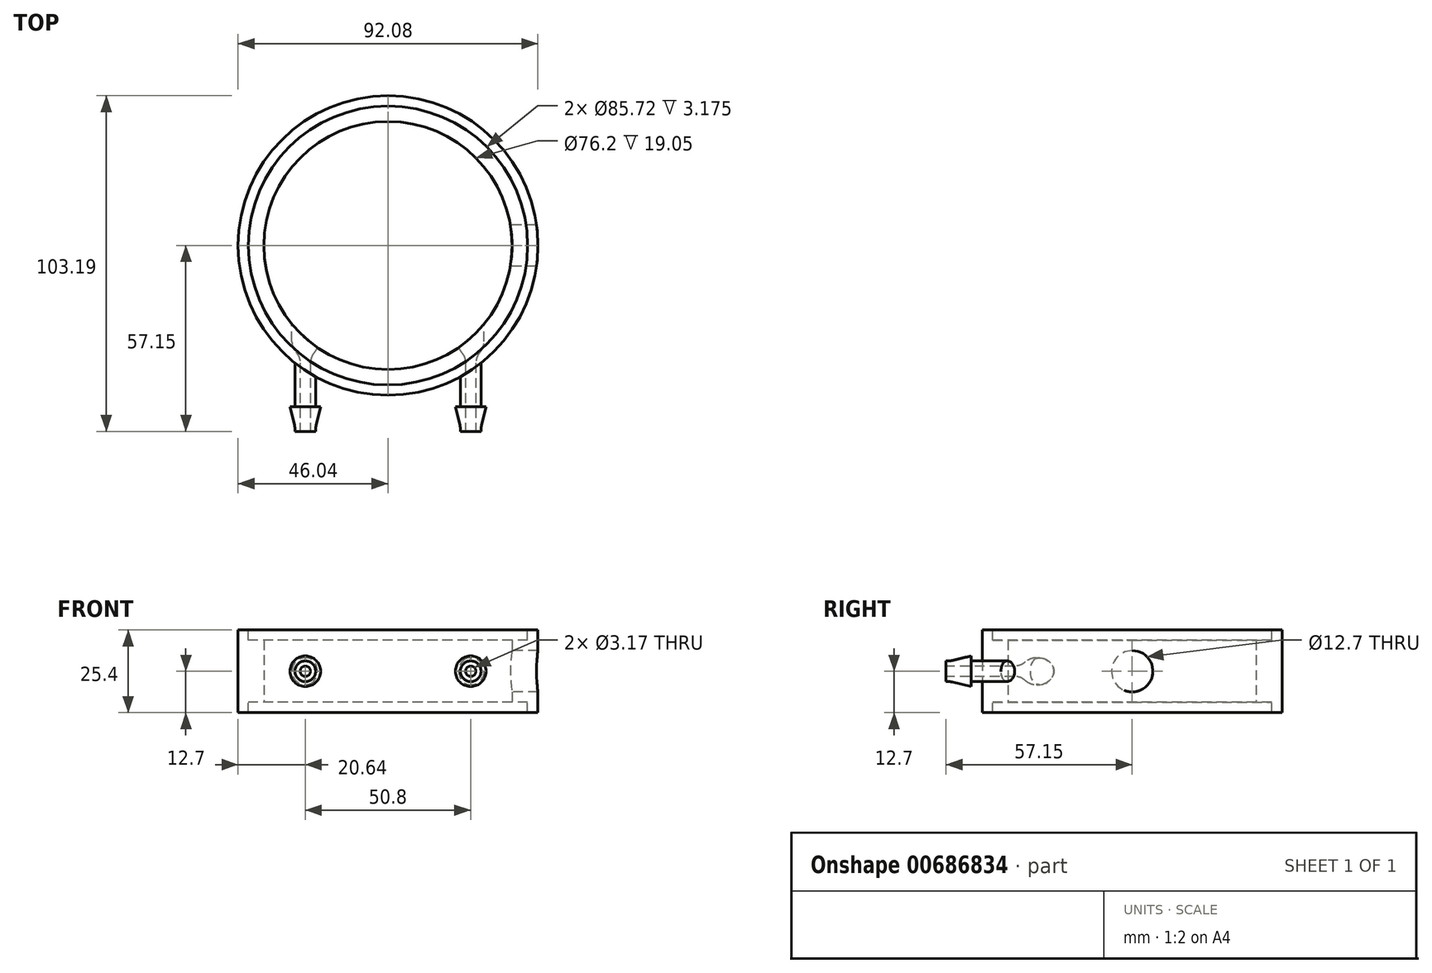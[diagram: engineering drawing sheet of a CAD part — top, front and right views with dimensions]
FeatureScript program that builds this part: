
annotation { "Feature Type Name" : "Feature", "Feature Type Description" : "" }
export const myFeature = defineFeature(function(context is Context, id is Id, definition is map)
    precondition{}
    {
        {
            var Q0;
            Q0=qCreatedBy(makeId("Top.planeOp"),FACE);
            var sketch = newSketch(context, id + "F0", { "sketchPlane" : qUnion([Q0])});
            skCircle(sketch, "E0", {"center": v(0, 0) * mm, "radius": 46.04 * mm});
            skSolve(sketch);
        }
        {
            var Q0;
            Q0 = qSketchRegion(id + "F0", true);
            extrude(context, id + "F1", {"entities" : qUnion([Q0]), "endBound" : BoundingType.SYMMETRIC, "depth" : 25.4 * mm, "offsetDistance" : 25.4 * mm});
        }
        {
            var Q0;
            Q0=qCreatedBy(makeId("Top.planeOp"),FACE);
            var sketch = newSketch(context, id + "F2", { "sketchPlane" : qUnion([Q0])});
            skCircle(sketch, "E1", {"center": v(0, 0) * mm, "radius": 42.86 * mm});
            skSolve(sketch);
        }
        {
            var Q0;
            Q0 = qSketchRegion(id + "F2", true);
            extrude(context, id + "F3", {"entities" : qUnion([Q0]), "operationType" : NewBodyOperationType.REMOVE, "endBound" : BoundingType.SYMMETRIC, "oppositeDirection" : true, "depth" : 25.4 * mm, "offsetDistance" : 25.4 * mm});
        }
        {
            var Q0;
            Q0=qCreatedBy(makeId("Top.planeOp"),FACE);
            var sketch = newSketch(context, id + "F4", { "sketchPlane" : qUnion([Q0])});
            skCircle(sketch, "E2", {"center": v(0, 0) * mm, "radius": 42.86 * mm});
            skSolve(sketch);
        }
        {
            var Q0;
            Q0 = qSketchRegion(id + "F4", true);
            extrude(context, id + "F5", {"entities" : qUnion([Q0]), "operationType" : NewBodyOperationType.ADD, "endBound" : BoundingType.SYMMETRIC, "depth" : 19.05 * mm, "offsetDistance" : 25.4 * mm});
        }
        {
            var Q0;
            Q0=qCreatedBy(makeId("Top.planeOp"),FACE);
            var sketch = newSketch(context, id + "F6", { "sketchPlane" : qUnion([Q0])});
            skCircle(sketch, "E3", {"center": v(0, 0) * mm, "radius": 38.1 * mm});
            skSolve(sketch);
        }
        {
            var Q0;
            Q0=qCreatedBy(makeId("Front.planeOp"),FACE);
            var sketch = newSketch(context, id + "F7", { "sketchPlane" : qUnion([Q0])});
            skCircle(sketch, "E4", {"center": v(-25.4, 0) * mm, "radius": 3.18 * mm});
            skSolve(sketch);
        }
        {
            var Q0;
            Q0=qCreatedBy(makeId("Front.planeOp"),FACE);
            var sketch = newSketch(context, id + "F8", { "sketchPlane" : qUnion([Q0])});
            skCircle(sketch, "E5", {"center": v(25.4, 0) * mm, "radius": 3.18 * mm});
            skSolve(sketch);
        }
        {
            var Q0;
            Q0 = qSketchRegion(id + "F7", true);
            extrude(context, id + "F9", {"entities" : qUnion([Q0]), "operationType" : NewBodyOperationType.ADD, "depth" : 57.15 * mm, "offsetDistance" : 25.4 * mm});
        }
        {
            var Q0;
            Q0 = qSketchRegion(id + "F8", true);
            extrude(context, id + "F10", {"entities" : qUnion([Q0]), "operationType" : NewBodyOperationType.ADD, "depth" : 57.15 * mm, "offsetDistance" : 25.4 * mm});
        }
        {
            var Q0;
            Q0=makeQuery(id+"F9.opExtrude","CAP_FACE",FACE,{"disambiguationData":[OSD([sQuery(id+"F7.wireOp",EDGE,"E4")])],"isStart":false});
            var sketch = newSketch(context, id + "F11", { "sketchPlane" : qUnion([Q0])});
            skCircle(sketch, "E6", {"center": v(-25.4, 0) * mm, "radius": 1.59 * mm});
            skSolve(sketch);
        }
        {
            var Q0;
            Q0=makeQuery(id+"F11.imprint","IMPRINT",FACE,{"disambiguationData":[TD([[makeQuery(id+"F11.imprint","IMPRINT",EDGE,{"derivedFrom":sQuery(id+"F11.wireOp",EDGE,"E6")}),1.0]])]});
            extrude(context, id + "F12", {"entities" : qUnion([Q0]), "operationType" : NewBodyOperationType.REMOVE, "oppositeDirection" : true, "depth" : 57.15 * mm, "offsetDistance" : 25.4 * mm});
        }
        {
            var Q0;
            Q0=makeQuery(id+"F10.opExtrude","CAP_FACE",FACE,{"disambiguationData":[OSD([sQuery(id+"F8.wireOp",EDGE,"E5")])],"isStart":false});
            var sketch = newSketch(context, id + "F13", { "sketchPlane" : qUnion([Q0])});
            skCircle(sketch, "E7", {"center": v(25.4, 0) * mm, "radius": 1.59 * mm});
            skSolve(sketch);
        }
        {
            var Q0;
            Q0=makeQuery(id+"F13.imprint","IMPRINT",FACE,{"disambiguationData":[TD([[makeQuery(id+"F13.imprint","IMPRINT",EDGE,{"derivedFrom":sQuery(id+"F13.wireOp",EDGE,"E7")}),1.0]])]});
            extrude(context, id + "F14", {"entities" : qUnion([Q0]), "operationType" : NewBodyOperationType.REMOVE, "oppositeDirection" : true, "depth" : 57.15 * mm, "offsetDistance" : 25.4 * mm});
        }
        {
            var Q0;
            Q0 = qSketchRegion(id + "F6", true);
            extrude(context, id + "F15", {"entities" : qUnion([Q0]), "operationType" : NewBodyOperationType.REMOVE, "endBound" : BoundingType.SYMMETRIC, "depth" : 25.4 * mm, "offsetDistance" : 25.4 * mm});
        }
        {
            var Q0;
            Q0=qCreatedBy(makeId("Top.planeOp"),FACE);
            var sketch = newSketch(context, id + "F16", { "sketchPlane" : qUnion([Q0])});
            skLineSegment(sketch, "E8", {"start": v(22.23, -49.53) * mm, "end": v(22.23, -55.88) * mm});
            skLineSegment(sketch, "E9", {"start": v(22.23, -49.53) * mm, "end": v(20.7, -49.53) * mm});
            skLineSegment(sketch, "E10", {"start": v(20.7, -49.53) * mm, "end": v(22.23, -55.88) * mm});
            skSolve(sketch);
        }
        {
            var Q0;
            Q0=makeQuery(id+"F16.imprint","IMPRINT",FACE,{"disambiguationData":[TD([[makeQuery(id+"F16.imprint","IMPRINT",EDGE,{"derivedFrom":sQuery(id+"F16.wireOp",EDGE,"E8")}),-1.0]])]});
            var Q1;
            Q1=makeQuery(id+"F10.opExtrude","CAP_EDGE",EDGE,{"disambiguationData":[OSD([sQuery(id+"F8.wireOp",EDGE,"E5")])],"isStart":false});
            revolve(context, id + "F17", {"operationType" : NewBodyOperationType.ADD, "entities" : qUnion([Q0]), "axis" : qUnion([Q1]), "revolveType" : RevolveType.FULL});
        }
        {
            var Q0;
            Q0=qCreatedBy(makeId("Top.planeOp"),FACE);
            var sketch = newSketch(context, id + "F18", { "sketchPlane" : qUnion([Q0])});
            skLineSegment(sketch, "E11", {"start": v(-22.23, -49.53) * mm, "end": v(-22.23, -55.88) * mm});
            skLineSegment(sketch, "E12", {"start": v(-22.23, -49.53) * mm, "end": v(-20.7, -49.53) * mm});
            skLineSegment(sketch, "E13", {"start": v(-20.7, -49.53) * mm, "end": v(-22.23, -55.88) * mm});
            skSolve(sketch);
        }
        {
            var Q0;
            Q0=makeQuery(id+"F18.imprint","IMPRINT",FACE,{"disambiguationData":[TD([[makeQuery(id+"F18.imprint","IMPRINT",EDGE,{"derivedFrom":sQuery(id+"F18.wireOp",EDGE,"E11")}),1.0]])]});
            var Q1;
            Q1=makeQuery(id+"F9.opExtrude","CAP_EDGE",EDGE,{"disambiguationData":[OSD([sQuery(id+"F7.wireOp",EDGE,"E4")])],"isStart":false});
            revolve(context, id + "F19", {"operationType" : NewBodyOperationType.ADD, "entities" : qUnion([Q0]), "axis" : qUnion([Q1]), "revolveType" : RevolveType.FULL});
        }
        {
            var Q0;
            Q0=makeQuery(id+"F19.opRevolve","SWEPT_EDGE",EDGE,{"disambiguationData":[OSD([sQuery(id+"F18.wireOp",EDGE,"E11"),sQuery(id+"F18.wireOp",EDGE,"E13")])]});
            fillet(context, id + "F20", {"entities" : qUnion([Q0]), "radius" : 5.08 * mm, "tangentPropagation" : true, "allowEdgeOverflow" : false});
        }
        {
            var Q0;
            Q0=makeQuery(id+"F17.opRevolve","SWEPT_EDGE",EDGE,{"disambiguationData":[OSD([sQuery(id+"F16.wireOp",EDGE,"E8"),sQuery(id+"F16.wireOp",EDGE,"E10")])]});
            fillet(context, id + "F21", {"entities" : qUnion([Q0]), "radius" : 5.08 * mm, "tangentPropagation" : true, "allowEdgeOverflow" : false});
        }
        {
            var Q0;
            Q0=qCreatedBy(makeId("Front.planeOp"),FACE);
            var sketch = newSketch(context, id + "F22", { "sketchPlane" : qUnion([Q0])});
            skCircle(sketch, "E14", {"center": v(-25.4, 0) * mm, "radius": 4.13 * mm});
            skSolve(sketch);
        }
        {
            var Q0;
            Q0=makeQuery(id+"F22.imprint","IMPRINT",FACE,{"disambiguationData":[TD([[makeQuery(id+"F22.imprint","IMPRINT",EDGE,{"derivedFrom":sQuery(id+"F22.wireOp",EDGE,"E14")}),1.0]])]});
            extrude(context, id + "F23", {"entities" : qUnion([Q0]), "operationType" : NewBodyOperationType.REMOVE, "depth" : 31.75 * mm, "offsetDistance" : 25.4 * mm});
        }
        {
            var Q0;
            Q0=makeQuery(id+"F23.boolean.opBoolean","INTERSECT",EDGE,{"derivedFrom":[makeQuery(id+"F12.boolean.opBoolean","COPY",FACE,{"derivedFrom":makeQuery(id+"F12.opExtrude","SWEPT_FACE",FACE,{"disambiguationData":[OSD([sQuery(id+"F11.wireOp",EDGE,"E6")])]})}),makeQuery(id+"F23.opExtrude","CAP_FACE",FACE,{"disambiguationData":[OSD([sQuery(id+"F22.wireOp",EDGE,"E14")])],"isStart":false})]});
            fillet(context, id + "F24", {"entities" : qUnion([Q0]), "radius" : 5.08 * mm, "tangentPropagation" : true, "allowEdgeOverflow" : false});
        }
        {
            var Q0;
            {var subQ0=sQuery(id+"F22.wireOp",EDGE,"E14");Q0=makeQuery(id+"F24.opFillet","BLEND_EDGE",EDGE,{"blendedFrom":[makeQuery(id+"F23.boolean.opBoolean","INTERSECT",EDGE,{"derivedFrom":[makeQuery(id+"F12.boolean.opBoolean","COPY",FACE,{"derivedFrom":makeQuery(id+"F12.opExtrude","SWEPT_FACE",FACE,{"disambiguationData":[OSD([sQuery(id+"F11.wireOp",EDGE,"E6")])]})}),makeQuery(id+"F23.opExtrude","CAP_FACE",FACE,{"disambiguationData":[OSD([subQ0])],"isStart":false})]}),makeQuery(id+"F23.boolean.opBoolean","COPY",FACE,{"derivedFrom":makeQuery(id+"F23.opExtrude","SWEPT_FACE",FACE,{"disambiguationData":[OSD([subQ0])]})})],"blendedInto":[makeQuery(id+"F23.boolean.opBoolean","COPY",FACE,{"derivedFrom":makeQuery(id+"F23.opExtrude","SWEPT_FACE",FACE,{"disambiguationData":[OSD([subQ0])]})})]});}
            fillet(context, id + "F25", {"entities" : qUnion([Q0]), "radius" : 5.08 * mm, "tangentPropagation" : true, "allowEdgeOverflow" : false});
        }
        {
            var Q0;
            Q0=qCreatedBy(makeId("Front.planeOp"),FACE);
            var sketch = newSketch(context, id + "F26", { "sketchPlane" : qUnion([Q0])});
            skCircle(sketch, "E15", {"center": v(25.4, 0) * mm, "radius": 4.13 * mm});
            skSolve(sketch);
        }
        {
            var Q0;
            Q0 = qSketchRegion(id + "F26", true);
            extrude(context, id + "F27", {"entities" : qUnion([Q0]), "operationType" : NewBodyOperationType.REMOVE, "depth" : 31.75 * mm, "offsetDistance" : 25.4 * mm});
        }
        {
            var Q0;
            Q0=makeQuery(id+"F27.boolean.opBoolean","INTERSECT",EDGE,{"derivedFrom":[makeQuery(id+"F14.boolean.opBoolean","COPY",FACE,{"derivedFrom":makeQuery(id+"F14.opExtrude","SWEPT_FACE",FACE,{"disambiguationData":[OSD([sQuery(id+"F13.wireOp",EDGE,"E7")])]})}),makeQuery(id+"F27.opExtrude","CAP_FACE",FACE,{"disambiguationData":[OSD([sQuery(id+"F26.wireOp",EDGE,"E15")])],"isStart":false})]});
            fillet(context, id + "F28", {"entities" : qUnion([Q0]), "radius" : 5.08 * mm, "tangentPropagation" : true, "allowEdgeOverflow" : false});
        }
        {
            var Q0;
            {var subQ0=sQuery(id+"F26.wireOp",EDGE,"E15");Q0=makeQuery(id+"F28.opFillet","BLEND_EDGE",EDGE,{"blendedFrom":[makeQuery(id+"F27.boolean.opBoolean","INTERSECT",EDGE,{"derivedFrom":[makeQuery(id+"F14.boolean.opBoolean","COPY",FACE,{"derivedFrom":makeQuery(id+"F14.opExtrude","SWEPT_FACE",FACE,{"disambiguationData":[OSD([sQuery(id+"F13.wireOp",EDGE,"E7")])]})}),makeQuery(id+"F27.opExtrude","CAP_FACE",FACE,{"disambiguationData":[OSD([subQ0])],"isStart":false})]}),makeQuery(id+"F27.boolean.opBoolean","COPY",FACE,{"derivedFrom":makeQuery(id+"F27.opExtrude","SWEPT_FACE",FACE,{"disambiguationData":[OSD([subQ0])]})})],"blendedInto":[makeQuery(id+"F27.boolean.opBoolean","COPY",FACE,{"derivedFrom":makeQuery(id+"F27.opExtrude","SWEPT_FACE",FACE,{"disambiguationData":[OSD([subQ0])]})})]});}
            fillet(context, id + "F29", {"entities" : qUnion([Q0]), "radius" : 5.08 * mm, "tangentPropagation" : true, "allowEdgeOverflow" : false});
        }
        {
            var Q0;
            Q0=qCreatedBy(makeId("Right.planeOp"),FACE);
            var sketch = newSketch(context, id + "F30", { "sketchPlane" : qUnion([Q0])});
            skCircle(sketch, "E16", {"center": v(0, 0) * mm, "radius": 6.35 * mm});
            skSolve(sketch);
        }
        {
            var Q0;
            Q0=makeQuery(id+"F30.imprint","IMPRINT",FACE,{"disambiguationData":[TD([[makeQuery(id+"F30.imprint","IMPRINT",EDGE,{"derivedFrom":sQuery(id+"F30.wireOp",EDGE,"E16")}),1.0]])]});
            var Q1;
            Q1=sQuery(id+"F30.wireOp",EDGE,"E16");
            extrude(context, id + "F31", {"entities" : qUnion([Q0]), "operationType" : NewBodyOperationType.REMOVE, "surfaceEntities" : qUnion([Q1]), "depth" : 76.2 * mm, "offsetDistance" : 25.4 * mm});
        }
    });
